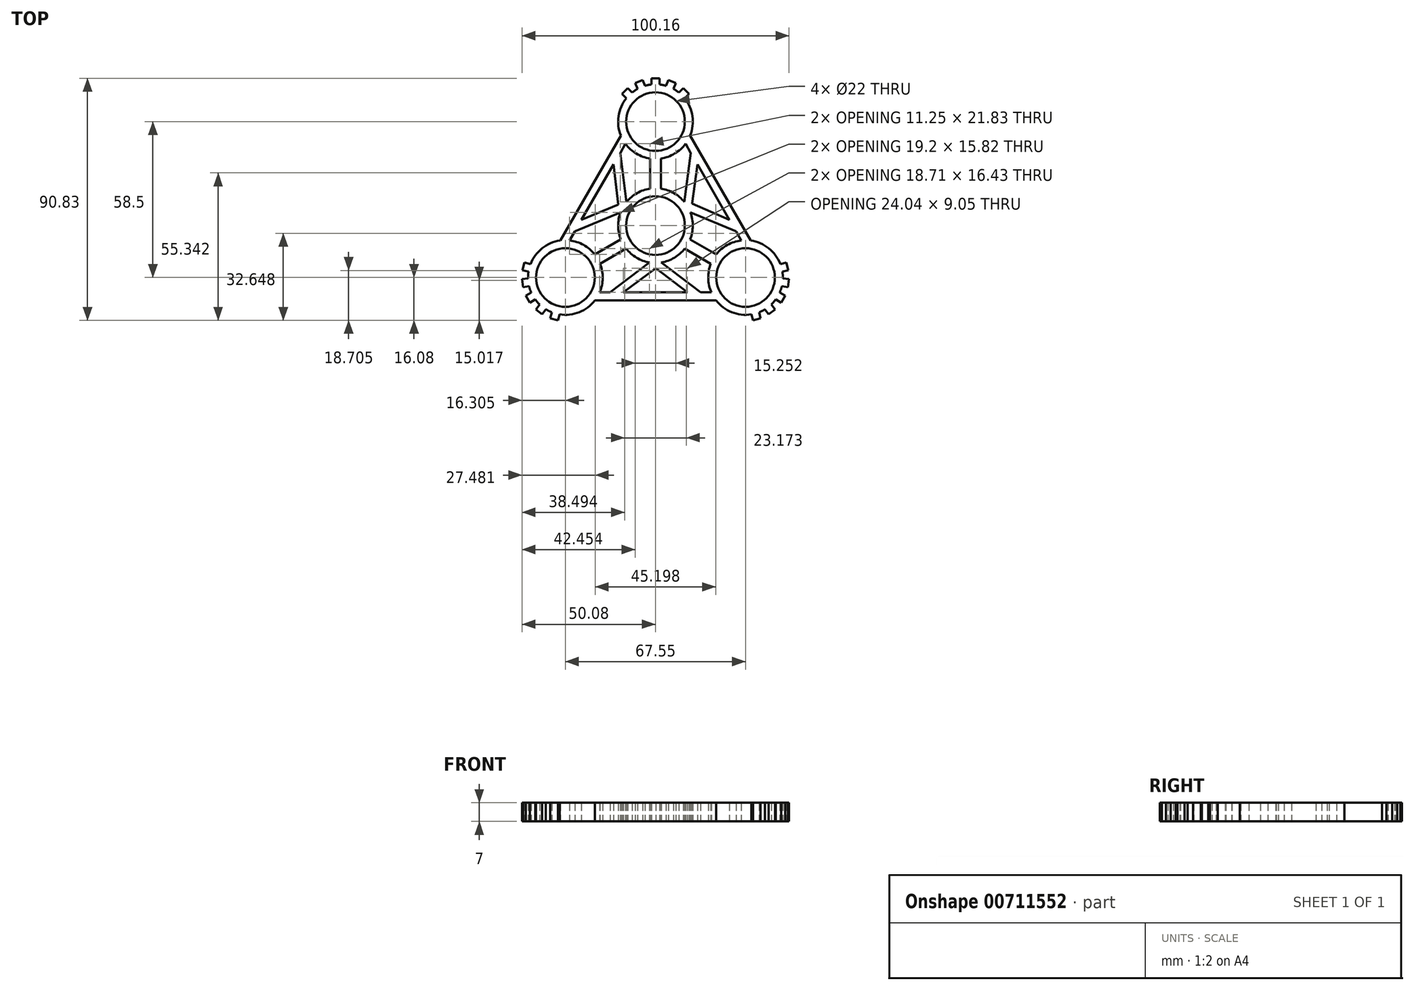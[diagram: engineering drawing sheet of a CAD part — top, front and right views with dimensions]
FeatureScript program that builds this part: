
annotation { "Feature Type Name" : "Feature", "Feature Type Description" : "" }
export const myFeature = defineFeature(function(context is Context, id is Id, definition is map)
    precondition{}
    {
        {
            var Q0;
            Q0=qCreatedBy(makeId("Top.planeOp"),FACE);
            var sketch = newSketch(context, id + "F0", { "sketchPlane" : qUnion([Q0])});
            skCircle(sketch, "E0", {"center": v(0, 0) * mm, "radius": 11 * mm});
            skArc(sketch, "E1.0", {"start": v(-2, 13.86) * mm, "mid": v(-6.9, 12.18) * mm, "end": v(-10.85, 8.84) * mm});
            skCircle(sketch, "E2", {"center": v(0, 39) * mm, "radius": 11 * mm});
            skArc(sketch, "E3.0", {"start": v(-10.9, 47.78) * mm, "mid": v(-13.85, 41.03) * mm, "end": v(-12.97, 33.72) * mm});
            skLineSegment(sketch, "E4", {"start": v(0, 11) * mm, "end": v(0, 28) * mm, "construction": true});
            skLineSegment(sketch, "E5.0", {"start": v(2, 13.86) * mm, "end": v(2, 25.14) * mm});
            skLineSegment(sketch, "E6.0", {"start": v(-2, 13.86) * mm, "end": v(-2, 25.14) * mm});
            skLineSegment(sketch, "E7", {"start": v(0, 53) * mm, "end": v(0, 55) * mm, "construction": true});
            skLineSegment(sketch, "E8.0", {"start": v(1.5, 52.92) * mm, "end": v(1.5, 55.25) * mm});
            skLineSegment(sketch, "E9.0", {"start": v(-1.5, 52.92) * mm, "end": v(-1.5, 55.25) * mm});
            skLineSegment(sketch, "E10", {"start": v(-1.5, 55.25) * mm, "end": v(1.5, 55.25) * mm});
            skLineSegment(sketch, "E11.1.0", {"start": v(4.83, 54.59) * mm, "end": v(7.6, 53.44) * mm});
            skLineSegment(sketch, "E11.1.1", {"start": v(3.94, 52.43) * mm, "end": v(4.83, 54.59) * mm});
            skLineSegment(sketch, "E11.1.2", {"start": v(6.71, 51.29) * mm, "end": v(7.6, 53.44) * mm});
            skLineSegment(sketch, "E11.2.0", {"start": v(10.43, 51.55) * mm, "end": v(12.55, 49.43) * mm});
            skLineSegment(sketch, "E11.2.1", {"start": v(8.78, 49.9) * mm, "end": v(10.43, 51.55) * mm});
            skLineSegment(sketch, "E11.2.2", {"start": v(10.9, 47.78) * mm, "end": v(12.55, 49.43) * mm});
            skLineSegment(sketch, "E11.anchor1", {"start": v(0, 39) * mm, "end": v(-1.5, 55.25) * mm, "construction": true});
            skLineSegment(sketch, "E11.anchor2", {"start": v(0, 39) * mm, "end": v(10.43, 51.55) * mm, "construction": true});
            skLineSegment(sketch, "E12.MirrorCS", {"start": v(-4.83, 54.59) * mm, "end": v(-7.6, 53.44) * mm});
            skLineSegment(sketch, "E13.MirrorCS", {"start": v(-3.94, 52.43) * mm, "end": v(-4.83, 54.59) * mm});
            skLineSegment(sketch, "E14.MirrorCS", {"start": v(-6.71, 51.29) * mm, "end": v(-7.6, 53.44) * mm});
            skLineSegment(sketch, "E15.MirrorCS", {"start": v(-8.78, 49.9) * mm, "end": v(-10.43, 51.55) * mm});
            skLineSegment(sketch, "E16.MirrorCS", {"start": v(-10.43, 51.55) * mm, "end": v(-12.55, 49.43) * mm});
            skLineSegment(sketch, "E17.MirrorCS", {"start": v(-10.9, 47.78) * mm, "end": v(-12.55, 49.43) * mm});
            skArc(sketch, "E18.trimOffspring", {"start": v(-6.71, 51.29) * mm, "mid": v(-7.78, 50.64) * mm, "end": v(-8.78, 49.9) * mm});
            skArc(sketch, "E19.trimOffspring", {"start": v(-1.29, 52.94) * mm, "mid": v(-2.63, 52.75) * mm, "end": v(-3.94, 52.43) * mm});
            skArc(sketch, "E20.trimOffspring", {"start": v(3.94, 52.43) * mm, "mid": v(2.73, 52.73) * mm, "end": v(1.5, 52.92) * mm});
            skArc(sketch, "E21.trimOffspring", {"start": v(8.95, 49.77) * mm, "mid": v(7.87, 50.58) * mm, "end": v(6.71, 51.29) * mm});
            skArc(sketch, "E22.trimOffspring", {"start": v(2, 25.14) * mm, "mid": v(7.18, 26.98) * mm, "end": v(11.26, 30.68) * mm});
            skLineSegment(sketch, "E23.1.0", {"start": v(-33.77, -19.5) * mm, "end": v(-47.1, -28.92) * mm, "construction": true});
            skPoint(sketch, "E23.1.1", {"position": v(-33.77, -19.5) * mm});
            skCircle(sketch, "E23.1.2", {"center": v(-33.77, -19.5) * mm, "radius": 11 * mm});
            skLineSegment(sketch, "E23.1.3", {"start": v(-9.53, -5.5) * mm, "end": v(-24.25, -14) * mm, "construction": true});
            skArc(sketch, "E23.1.4", {"start": v(-35.93, -33.33) * mm, "mid": v(-28.6, -32.51) * mm, "end": v(-22.72, -28.09) * mm});
            skLineSegment(sketch, "E23.1.5", {"start": v(-13, -5.2) * mm, "end": v(-22.77, -10.84) * mm});
            skLineSegment(sketch, "E23.1.6", {"start": v(-11, -8.66) * mm, "end": v(-20.77, -14.3) * mm});
            skLineSegment(sketch, "E23.1.7", {"start": v(-33.77, -19.5) * mm, "end": v(-49.86, -16.74) * mm, "construction": true});
            skArc(sketch, "E23.1.8", {"start": v(-22.77, -10.84) * mm, "mid": v(-26.96, -7.27) * mm, "end": v(-32.2, -5.59) * mm});
            skLineSegment(sketch, "E23.1.9", {"start": v(-41.06, -31.46) * mm, "end": v(-42.48, -33.3) * mm});
            skLineSegment(sketch, "E23.1.10", {"start": v(-35.93, -33.33) * mm, "end": v(-36.53, -35.58) * mm});
            skLineSegment(sketch, "E23.1.11", {"start": v(-49.86, -16.74) * mm, "end": v(-49.08, -13.85) * mm});
            skLineSegment(sketch, "E23.1.12", {"start": v(-47.77, -19.83) * mm, "end": v(-50.08, -20.13) * mm});
            skArc(sketch, "E23.1.13", {"start": v(-47.57, -17.13) * mm, "mid": v(-47.74, -18.48) * mm, "end": v(-47.77, -19.83) * mm});
            skLineSegment(sketch, "E23.1.14", {"start": v(-44.86, -31.48) * mm, "end": v(-42.48, -33.3) * mm});
            skLineSegment(sketch, "E23.1.15", {"start": v(-45.9, -26.5) * mm, "end": v(-47.63, -27.5) * mm, "construction": true});
            skLineSegment(sketch, "E23.1.16", {"start": v(-46.58, -25.16) * mm, "end": v(-48.6, -26.33) * mm});
            skLineSegment(sketch, "E23.1.17", {"start": v(-47.1, -28.92) * mm, "end": v(-48.6, -26.33) * mm});
            skLineSegment(sketch, "E23.1.18", {"start": v(-45.08, -27.76) * mm, "end": v(-47.1, -28.92) * mm});
            skLineSegment(sketch, "E23.1.19", {"start": v(-49.7, -23.1) * mm, "end": v(-50.08, -20.13) * mm});
            skLineSegment(sketch, "E23.1.20", {"start": v(-47.38, -22.8) * mm, "end": v(-49.7, -23.1) * mm});
            skArc(sketch, "E23.1.21", {"start": v(-47.38, -22.8) * mm, "mid": v(-47.03, -24) * mm, "end": v(-46.58, -25.16) * mm});
            skArc(sketch, "E23.1.22", {"start": v(-41.06, -31.46) * mm, "mid": v(-39.97, -32.06) * mm, "end": v(-38.83, -32.56) * mm});
            skLineSegment(sketch, "E23.1.23", {"start": v(-39.43, -34.8) * mm, "end": v(-36.53, -35.58) * mm});
            skLineSegment(sketch, "E23.1.24", {"start": v(-43.44, -29.63) * mm, "end": v(-44.86, -31.48) * mm});
            skLineSegment(sketch, "E23.1.25", {"start": v(-46.83, -14.45) * mm, "end": v(-49.08, -13.85) * mm});
            skArc(sketch, "E23.1.26", {"start": v(-45.2, -27.58) * mm, "mid": v(-44.37, -28.65) * mm, "end": v(-43.44, -29.63) * mm});
            skLineSegment(sketch, "E23.1.27", {"start": v(-38.83, -32.56) * mm, "end": v(-39.43, -34.8) * mm});
            skLineSegment(sketch, "E23.1.28", {"start": v(-47.6, -17.35) * mm, "end": v(-49.86, -16.74) * mm});
            skLineSegment(sketch, "E23.2.0", {"start": v(33.77, -19.5) * mm, "end": v(48.6, -26.33) * mm, "construction": true});
            skPoint(sketch, "E23.2.1", {"position": v(33.77, -19.5) * mm});
            skCircle(sketch, "E23.2.2", {"center": v(33.77, -19.5) * mm, "radius": 11 * mm});
            skLineSegment(sketch, "E23.2.3", {"start": v(9.53, -5.5) * mm, "end": v(24.25, -14) * mm, "construction": true});
            skArc(sketch, "E23.2.4", {"start": v(46.83, -14.45) * mm, "mid": v(42.46, -8.52) * mm, "end": v(35.69, -5.63) * mm});
            skLineSegment(sketch, "E23.2.5", {"start": v(11, -8.66) * mm, "end": v(20.77, -14.3) * mm});
            skLineSegment(sketch, "E23.2.6", {"start": v(13, -5.2) * mm, "end": v(22.77, -10.84) * mm});
            skLineSegment(sketch, "E23.2.7", {"start": v(33.77, -19.5) * mm, "end": v(39.43, -34.8) * mm, "construction": true});
            skArc(sketch, "E23.2.8", {"start": v(20.77, -14.3) * mm, "mid": v(19.78, -19.71) * mm, "end": v(20.94, -25.09) * mm});
            skLineSegment(sketch, "E23.2.9", {"start": v(47.77, -19.83) * mm, "end": v(50.08, -20.13) * mm});
            skLineSegment(sketch, "E23.2.10", {"start": v(46.83, -14.45) * mm, "end": v(49.08, -13.85) * mm});
            skLineSegment(sketch, "E23.2.11", {"start": v(39.43, -34.8) * mm, "end": v(36.53, -35.58) * mm});
            skLineSegment(sketch, "E23.2.12", {"start": v(41.06, -31.46) * mm, "end": v(42.48, -33.3) * mm});
            skArc(sketch, "E23.2.13", {"start": v(38.63, -32.63) * mm, "mid": v(39.87, -32.1) * mm, "end": v(41.06, -31.46) * mm});
            skLineSegment(sketch, "E23.2.14", {"start": v(49.7, -23.1) * mm, "end": v(50.08, -20.13) * mm});
            skLineSegment(sketch, "E23.2.15", {"start": v(45.9, -26.5) * mm, "end": v(47.63, -27.5) * mm, "construction": true});
            skLineSegment(sketch, "E23.2.16", {"start": v(45.08, -27.76) * mm, "end": v(47.1, -28.92) * mm});
            skLineSegment(sketch, "E23.2.17", {"start": v(48.6, -26.33) * mm, "end": v(47.1, -28.92) * mm});
            skLineSegment(sketch, "E23.2.18", {"start": v(46.58, -25.16) * mm, "end": v(48.6, -26.33) * mm});
            skLineSegment(sketch, "E23.2.19", {"start": v(44.86, -31.48) * mm, "end": v(42.48, -33.3) * mm});
            skLineSegment(sketch, "E23.2.20", {"start": v(43.44, -29.63) * mm, "end": v(44.86, -31.48) * mm});
            skArc(sketch, "E23.2.21", {"start": v(43.44, -29.63) * mm, "mid": v(44.3, -28.73) * mm, "end": v(45.08, -27.76) * mm});
            skArc(sketch, "E23.2.22", {"start": v(47.77, -19.83) * mm, "mid": v(47.75, -18.58) * mm, "end": v(47.6, -17.35) * mm});
            skLineSegment(sketch, "E23.2.23", {"start": v(49.86, -16.74) * mm, "end": v(49.08, -13.85) * mm});
            skLineSegment(sketch, "E23.2.24", {"start": v(47.38, -22.8) * mm, "end": v(49.7, -23.1) * mm});
            skLineSegment(sketch, "E23.2.25", {"start": v(35.93, -33.33) * mm, "end": v(36.53, -35.58) * mm});
            skArc(sketch, "E23.2.26", {"start": v(46.5, -25.36) * mm, "mid": v(47, -24.1) * mm, "end": v(47.38, -22.8) * mm});
            skLineSegment(sketch, "E23.2.27", {"start": v(47.6, -17.35) * mm, "end": v(49.86, -16.74) * mm});
            skLineSegment(sketch, "E23.2.28", {"start": v(38.83, -32.56) * mm, "end": v(39.43, -34.8) * mm});
            skArc(sketch, "E24.trimOffspring", {"start": v(13, -5.2) * mm, "mid": v(14, -0.12) * mm, "end": v(13.09, 4.98) * mm});
            skArc(sketch, "E25.trimOffspring", {"start": v(-11, -8.66) * mm, "mid": v(-7.1, -12.06) * mm, "end": v(-2.23, -13.82) * mm});
            skLineSegment(sketch, "E26", {"start": v(-12.97, 33.72) * mm, "end": v(-35.69, -5.63) * mm});
            skLineSegment(sketch, "E27.0", {"start": v(-11.26, 30.68) * mm, "end": v(-13.25, 27.23) * mm});
            skArc(sketch, "E28.trimOffspring", {"start": v(-11.26, 30.68) * mm, "mid": v(-7.18, 26.98) * mm, "end": v(-2, 25.14) * mm});
            skArc(sketch, "E29.trimOffspring", {"start": v(-35.69, -5.63) * mm, "mid": v(-42.46, -8.52) * mm, "end": v(-46.83, -14.45) * mm});
            skLineSegment(sketch, "E30", {"start": v(-12.12, 7) * mm, "end": v(-28.97, 0) * mm, "construction": true});
            skLineSegment(sketch, "E31", {"start": v(-12.12, 7) * mm, "end": v(-21.73, 12.54) * mm, "construction": true});
            skLineSegment(sketch, "E32.0", {"start": v(-13.98, 7.85) * mm, "end": v(-27.74, 2.14) * mm});
            skLineSegment(sketch, "E33.0", {"start": v(-13.09, 4.98) * mm, "end": v(-30.2, -2.14) * mm});
            skLineSegment(sketch, "E34.trimOffspring", {"start": v(-30.2, -2.14) * mm, "end": v(-32.2, -5.59) * mm});
            skArc(sketch, "E35.trimOffspring", {"start": v(-13.09, 4.98) * mm, "mid": v(-14, -0.12) * mm, "end": v(-13, -5.2) * mm});
            skLineSegment(sketch, "E36.MirrorCS", {"start": v(-10.85, 8.84) * mm, "end": v(-13.25, 27.23) * mm});
            skLineSegment(sketch, "E37.trimOffspring", {"start": v(-15.72, 22.95) * mm, "end": v(-27.74, 2.14) * mm});
            skPoint(sketch, "E38.orphan", {"position": v(-10.45, 9.32) * mm});
            skLineSegment(sketch, "E39.trimOffspring", {"start": v(-13.98, 7.85) * mm, "end": v(-15.72, 22.95) * mm});
            skPoint(sketch, "E40.MirrorCS.start.orphan", {"position": v(-13.3, 4.38) * mm});
            skLineSegment(sketch, "E41.1.0", {"start": v(-22.72, -28.09) * mm, "end": v(22.72, -28.09) * mm});
            skLineSegment(sketch, "E41.1.1", {"start": v(0.2, -16.04) * mm, "end": v(-12.02, -25.09) * mm});
            skLineSegment(sketch, "E41.1.2", {"start": v(0, -14) * mm, "end": v(0, -25.09) * mm, "construction": true});
            skLineSegment(sketch, "E41.1.3", {"start": v(-12.02, -25.09) * mm, "end": v(12.02, -25.09) * mm});
            skLineSegment(sketch, "E41.1.4", {"start": v(-2.23, -13.82) * mm, "end": v(-16.95, -25.09) * mm});
            skLineSegment(sketch, "E41.1.5", {"start": v(16.95, -25.09) * mm, "end": v(20.94, -25.09) * mm});
            skLineSegment(sketch, "E41.1.6", {"start": v(2.23, -13.82) * mm, "end": v(16.95, -25.09) * mm});
            skLineSegment(sketch, "E41.1.7", {"start": v(0.2, -16.04) * mm, "end": v(12.02, -25.09) * mm});
            skLineSegment(sketch, "E41.1.8", {"start": v(0, -14) * mm, "end": v(14.49, -25.09) * mm, "construction": true});
            skLineSegment(sketch, "E41.1.9", {"start": v(-20.94, -25.09) * mm, "end": v(-16.95, -25.09) * mm});
            skLineSegment(sketch, "E41.2.0", {"start": v(35.69, -5.63) * mm, "end": v(12.97, 33.72) * mm});
            skLineSegment(sketch, "E41.2.1", {"start": v(13.8, 8.18) * mm, "end": v(27.74, 2.14) * mm});
            skLineSegment(sketch, "E41.2.2", {"start": v(12.12, 7) * mm, "end": v(21.73, 12.54) * mm, "construction": true});
            skLineSegment(sketch, "E41.2.3", {"start": v(27.74, 2.14) * mm, "end": v(15.72, 22.95) * mm});
            skLineSegment(sketch, "E41.2.4", {"start": v(13.09, 4.98) * mm, "end": v(30.2, -2.14) * mm});
            skLineSegment(sketch, "E41.2.5", {"start": v(13.25, 27.23) * mm, "end": v(11.26, 30.68) * mm});
            skLineSegment(sketch, "E41.2.6", {"start": v(10.85, 8.84) * mm, "end": v(13.25, 27.23) * mm});
            skLineSegment(sketch, "E41.2.7", {"start": v(13.8, 8.18) * mm, "end": v(15.72, 22.95) * mm});
            skLineSegment(sketch, "E41.2.8", {"start": v(12.12, 7) * mm, "end": v(14.49, 25.09) * mm, "construction": true});
            skLineSegment(sketch, "E41.2.9", {"start": v(32.2, -5.59) * mm, "end": v(30.2, -2.14) * mm});
            skArc(sketch, "E42.trimOffspring", {"start": v(12.97, 33.72) * mm, "mid": v(13.85, 41.03) * mm, "end": v(10.9, 47.78) * mm});
            skArc(sketch, "E43.trimOffspring", {"start": v(32.2, -5.59) * mm, "mid": v(26.96, -7.27) * mm, "end": v(22.77, -10.84) * mm});
            skArc(sketch, "E44.trimOffspring", {"start": v(10.85, 8.84) * mm, "mid": v(6.9, 12.18) * mm, "end": v(2, 13.86) * mm});
            skArc(sketch, "E45.trimOffspring", {"start": v(2.23, -13.82) * mm, "mid": v(7.1, -12.06) * mm, "end": v(11, -8.66) * mm});
            skArc(sketch, "E46.trimOffspring", {"start": v(22.72, -28.09) * mm, "mid": v(28.6, -32.51) * mm, "end": v(35.93, -33.33) * mm});
            skArc(sketch, "E47.trimOffspring", {"start": v(-20.94, -25.09) * mm, "mid": v(-19.78, -19.71) * mm, "end": v(-20.77, -14.3) * mm});
            skSolve(sketch);
        }
        {
            var Q0;
            Q0=qSketchRegion(id+"F0",true);
            extrude(context, id + "F1", {"entities" : qUnion([Q0]), "depth" : 7 * mm});
        }
    });
